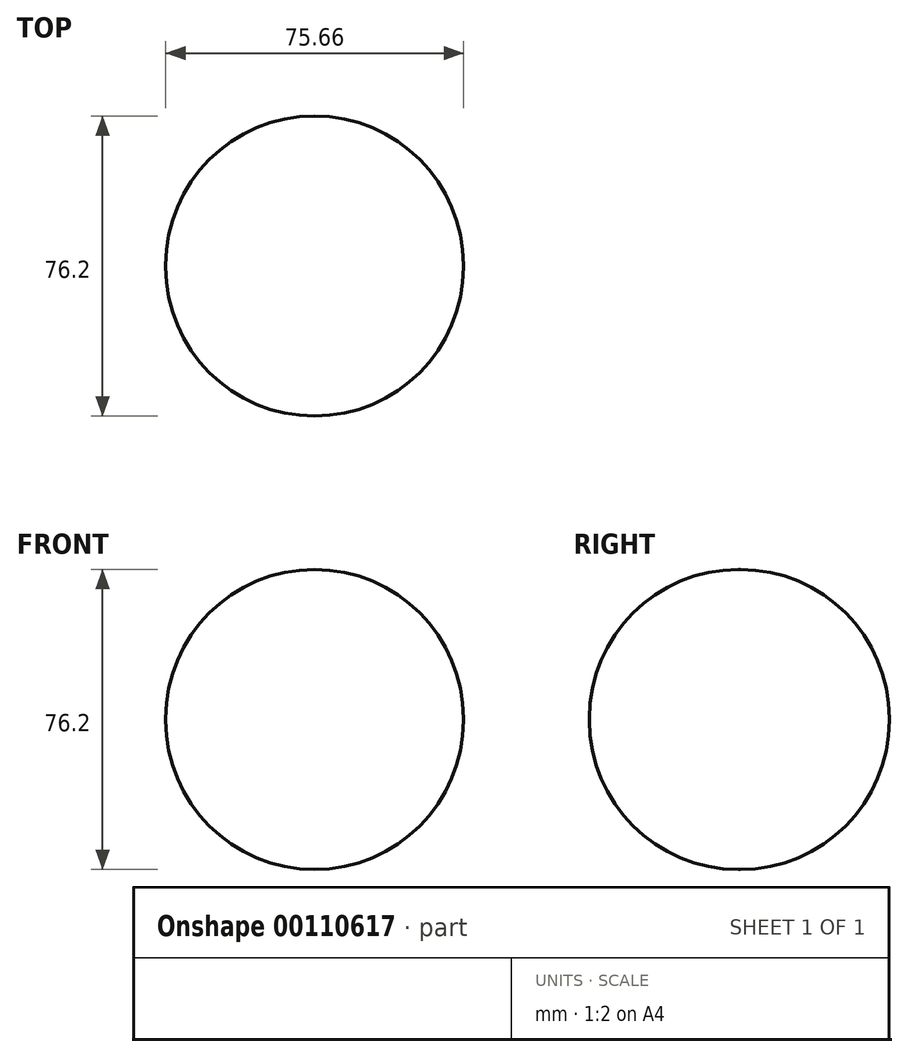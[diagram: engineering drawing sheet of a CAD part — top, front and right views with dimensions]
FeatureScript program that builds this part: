
annotation { "Feature Type Name" : "Feature", "Feature Type Description" : "" }
export const myFeature = defineFeature(function(context is Context, id is Id, definition is map)
    precondition{}
    {
        {
            var Q0;
            Q0=qCreatedBy(makeId("Top.planeOp"),FACE);
            var sketch = newSketch(context, id + "F1", { "sketchPlane" : qUnion([Q0])});
            skLineSegment(sketch, "E0.bottom", {"start": v(0, 0) * mm, "end": v(75.66, 0) * mm});
            skLineSegment(sketch, "E0.top", {"start": v(0, 76.2) * mm, "end": v(75.66, 76.2) * mm});
            skLineSegment(sketch, "E0.left", {"start": v(0, 0) * mm, "end": v(0, 76.2) * mm});
            skLineSegment(sketch, "E0.right", {"start": v(75.66, 0) * mm, "end": v(75.66, 76.2) * mm});
            skSolve(sketch);
        }
        {
            var Q0;
            Q0=makeQuery(id+"F1.imprint","IMPRINT",FACE,{"disambiguationData":[TD([[makeQuery(id+"F1.imprint","IMPRINT",EDGE,{"derivedFrom":sQuery(id+"F1.wireOp",EDGE,"E0.bottom")}),1.0]])]});
            extrude(context, id + "F0", {"entities" : qUnion([Q0]), "depth" : 76.2 * mm});
        }
        {
            var Q0;
            Q0=makeQuery(id+"F0.opExtrude","CAP_EDGE",EDGE,{"disambiguationData":[OSD([sQuery(id+"F1.wireOp",EDGE,"E0.bottom")])],"isStart":false});
            var Q1;
            Q1=makeQuery(id+"F0.opExtrude","CAP_EDGE",EDGE,{"disambiguationData":[OSD([sQuery(id+"F1.wireOp",EDGE,"E0.right")])],"isStart":false});
            var Q2;
            Q2=makeQuery(id+"F0.opExtrude","CAP_EDGE",EDGE,{"disambiguationData":[OSD([sQuery(id+"F1.wireOp",EDGE,"E0.top")])],"isStart":false});
            var Q3;
            Q3=makeQuery(id+"F0.opExtrude","CAP_EDGE",EDGE,{"disambiguationData":[OSD([sQuery(id+"F1.wireOp",EDGE,"E0.left")])],"isStart":false});
            var Q4;
            Q4=makeQuery(id+"F0.opExtrude","CAP_EDGE",EDGE,{"disambiguationData":[OSD([sQuery(id+"F1.wireOp",EDGE,"E0.bottom")])],"isStart":true});
            var Q5;
            Q5=makeQuery(id+"F0.opExtrude","CAP_EDGE",EDGE,{"disambiguationData":[OSD([sQuery(id+"F1.wireOp",EDGE,"E0.right")])],"isStart":true});
            var Q6;
            Q6=makeQuery(id+"F0.opExtrude","SWEPT_EDGE",EDGE,{"disambiguationData":[OSD([sQuery(id+"F1.wireOp",EDGE,"E0.bottom"),sQuery(id+"F1.wireOp",EDGE,"E0.right")])]});
            var Q7;
            Q7=makeQuery(id+"F0.opExtrude","SWEPT_EDGE",EDGE,{"disambiguationData":[OSD([sQuery(id+"F1.wireOp",EDGE,"E0.top"),sQuery(id+"F1.wireOp",EDGE,"E0.right")])]});
            var Q8;
            Q8=makeQuery(id+"F0.opExtrude","SWEPT_EDGE",EDGE,{"disambiguationData":[OSD([sQuery(id+"F1.wireOp",EDGE,"E0.bottom"),sQuery(id+"F1.wireOp",EDGE,"E0.left")])]});
            var Q9;
            Q9=makeQuery(id+"F0.opExtrude","CAP_EDGE",EDGE,{"disambiguationData":[OSD([sQuery(id+"F1.wireOp",EDGE,"E0.left")])],"isStart":true});
            var Q10;
            Q10=makeQuery(id+"F0.opExtrude","SWEPT_EDGE",EDGE,{"disambiguationData":[OSD([sQuery(id+"F1.wireOp",EDGE,"E0.top"),sQuery(id+"F1.wireOp",EDGE,"E0.left")])]});
            var Q11;
            Q11=makeQuery(id+"F0.opExtrude","CAP_EDGE",EDGE,{"disambiguationData":[OSD([sQuery(id+"F1.wireOp",EDGE,"E0.top")])],"isStart":true});
            fillet(context, id + "F2", {"entities" : qUnion([Q0, Q1, Q2, Q3, Q4, Q5, Q6, Q7, Q8, Q9, Q10, Q11]), "radius" : 37.83 * mm, "tangentPropagation" : true, "allowEdgeOverflow" : false});
        }
    });
